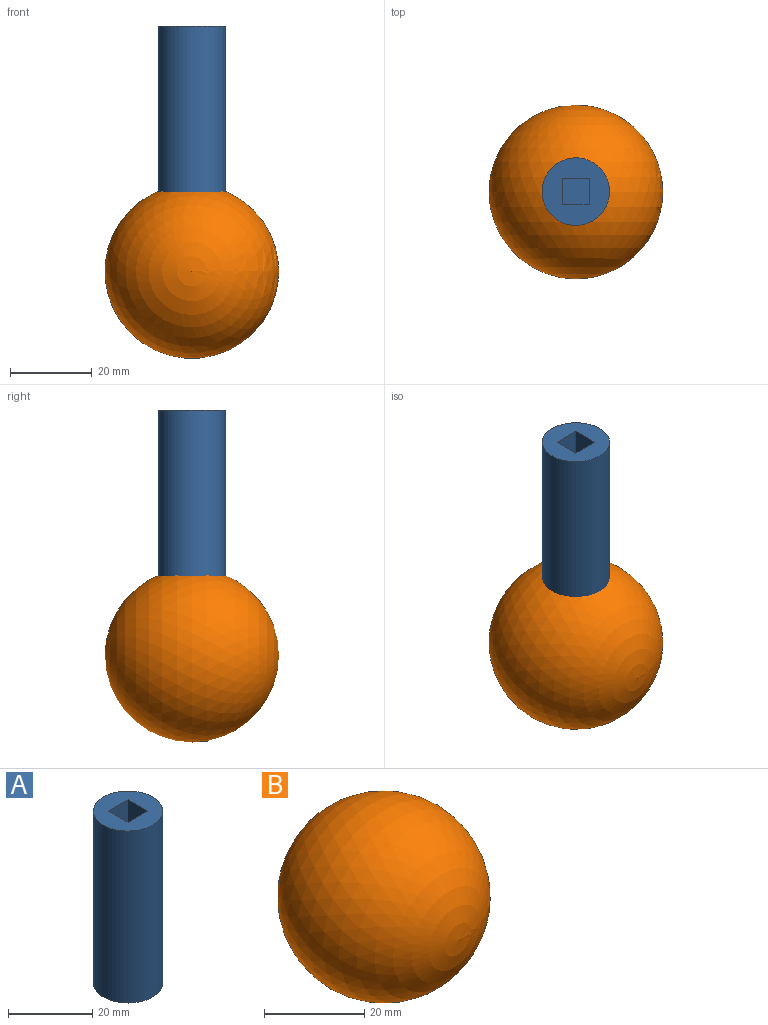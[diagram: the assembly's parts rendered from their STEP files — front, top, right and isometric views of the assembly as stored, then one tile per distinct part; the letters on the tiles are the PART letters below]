
ASSEMBLY  parts=2 mates=1
PART A: 8 faces, bbox 16.5x16.5x50 mm
  f0: cylinder r=8.25mm len=50mm, axis (0,0,-1), area 2591.8mm2, adj f1,f2
  f1: plane 16.5x16.5mm, normal (0,0,1), area 171.6mm2, adj f0,f3,f4,f5,f6
  f2: plane 16.5x16.5mm, normal (0,0,-1), area 213.8mm2, adj f0
  f3: plane 35x6.5mm, normal (-1,0,0), area 227.5mm2, adj f1,f4,f6,f7
  f4: plane 35x6.5mm, normal (0,-1,0), area 227.5mm2, adj f1,f3,f5,f7
  f5: plane 35x6.5mm, normal (1,0,0), area 227.5mm2, adj f1,f4,f6,f7
  f6: plane 35x6.5mm, normal (0,1,0), area 227.5mm2, adj f1,f3,f5,f7
  f7: plane 6.5x6.5mm, normal (0,0,1), area 42.2mm2, adj f3,f4,f5,f6
PART B: 1 faces, bbox 42.5x42.5x42.5 mm
  f0: sphere r=21.25mm, area 5674.5mm2
PLACE A t=(-36.97,103.71,-47.76)mm
PLACE B t=(30.67,104.44,-57.76)mm
MATE pin_slot A.f0 <-> B.f0  axis (0,0,-1) through (-36.97,103.71,-47.76)mm
